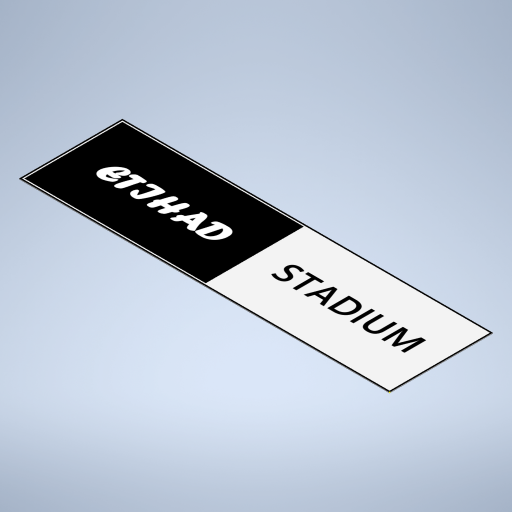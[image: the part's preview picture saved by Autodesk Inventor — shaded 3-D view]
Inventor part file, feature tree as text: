
AUTODESK INVENTOR PART (.ipt)
format: ipt  version: 2024.1 (Build 281209000, 209)  size: 268,800 bytes
history: native  units: in
note: dims shown in document units (in); Inventor stores cm internally (conversion verified against a paired STEP export)
features: extrude x3, sketch x2
ambient origin geometry x8: Origin, YZ Plane, XZ Plane, XY Plane, X Axis, Y Axis, Z Axis, Center Point
bodies: Solid6 (feature_tree), Solid7 (feature_tree)
feature tree (5):
  sketch  "Sketch2"  dims[d20=5.0in d21=0.0in d22=5.0in d23=0.0in]
  extrude  "Extrusion5"  Depth=5.0in TaperAngle=0.0deg
  extrude  "Extrusion6"  Depth=5.0in
  extrude  "Extrusion7"  Depth=5.0in
  sketch  "Sketch3"  dims[d24=5.0in d25=0.0in d7=0.5in d8=0.0344in d9=0.5in d10=0.0344in]
